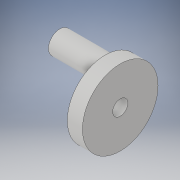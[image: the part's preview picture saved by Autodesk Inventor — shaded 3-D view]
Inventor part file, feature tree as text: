
AUTODESK INVENTOR PART (.ipt)
format: ipt  version: 2019 (Build 230136000, 136)  size: 111,104 bytes
history: native  units: in
note: dims shown in document units (in); Inventor stores cm internally (conversion verified against a paired STEP export)
features: sketch x2, revolve x1, extrude x1
ambient origin geometry x8: Origin, YZ Plane, XZ Plane, XY Plane, X Axis, Y Axis, Z Axis, Center Point
bodies: Solid1 (feature_tree)
feature tree (4):
  revolve  "Revolution1"  [1 undecoded]
  extrude  "Extrusion1"  Depth=0.3937in
  sketch  "Sketch1"  dims[d1=0.7874in d2=0.3937in]
  sketch  "Sketch2"  dims[d3=0.1969in d4=0.3937in d5=0.3937in d6=90.0deg d7=0.5906in d8=1.1811in d9=0.0in]
note: 1 required parameter value undecoded (feature->parameter linkage not recoverable at this tier; creation-order binding heuristic only, values carry confidence <= 0.55)
